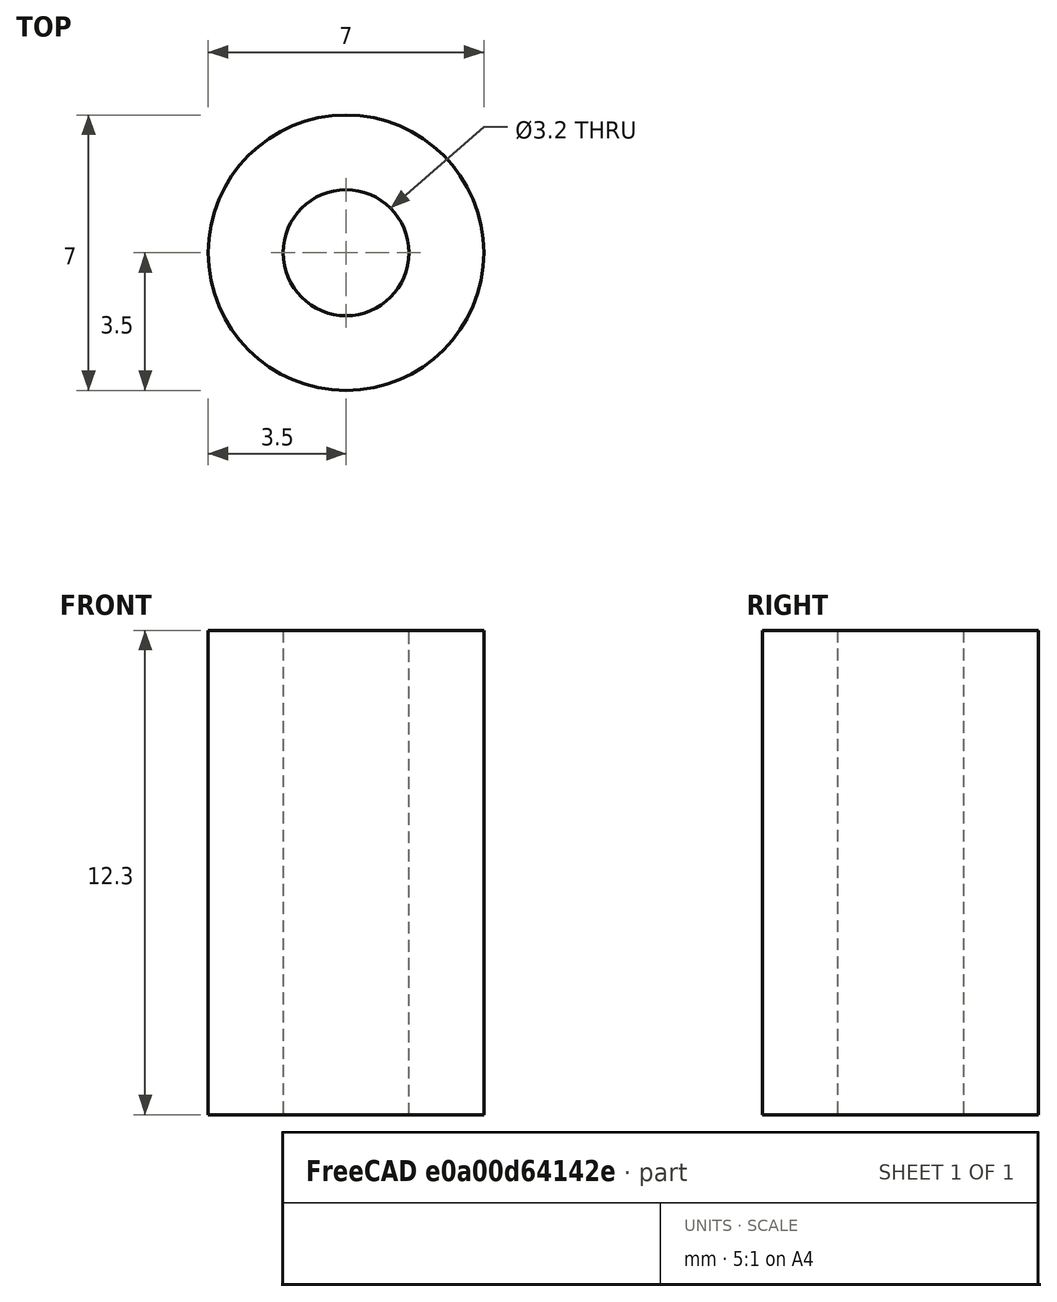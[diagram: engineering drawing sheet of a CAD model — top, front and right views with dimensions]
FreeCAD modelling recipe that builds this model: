
FCSTD DOCUMENT  (FreeCAD 0.21R33771 (Git))
Label: PCB-Spacer
License: All rights reserved
LicenseURL: https://en.wikipedia.org/wiki/All_rights_reserved
objects: Sketcher::SketchObject×1, PartDesign::Pad×1, PartDesign::Body×1
note: 4 computed .brp shape members not serialized (recipe doc carries the construction recipe); baked Part::Feature solids carry a one-line shape summary decoded from their .brp

FEATURE [Sketcher::SketchObject] Sketch
  FullyConstrained = true
  MapMode = 5
  Support = -> [XY_Plane]
  sketch-geometry (2):
    g0: Circle CenterX=0 CenterY=0 CenterZ=0 NormalX=0 NormalY=0 NormalZ=1 AngleXU=0 Radius=3.5
    g1: Circle CenterX=0 CenterY=0 CenterZ=0 NormalX=0 NormalY=0 NormalZ=1 AngleXU=0 Radius=1.6
  constraints (4):
    c: Coincident(g0,g-1)
    c: Coincident(g1,g0)
    c: Diameter(g0) = 7
    c: Diameter(g1) = 3.2
FEATURE [PartDesign::Pad] Pad
  Direction = (0,0,1)
  Length = 12.3
  Length2 = 10
  Profile = -> Sketch
  ReferenceAxis = -> Sketch [N_Axis]
  Type = 0
FEATURE [PartDesign::Body] Body  label="Spacer"
  Group = -> [Sketch,Pad]
  Origin = -> Origin
  Tip = -> Pad
